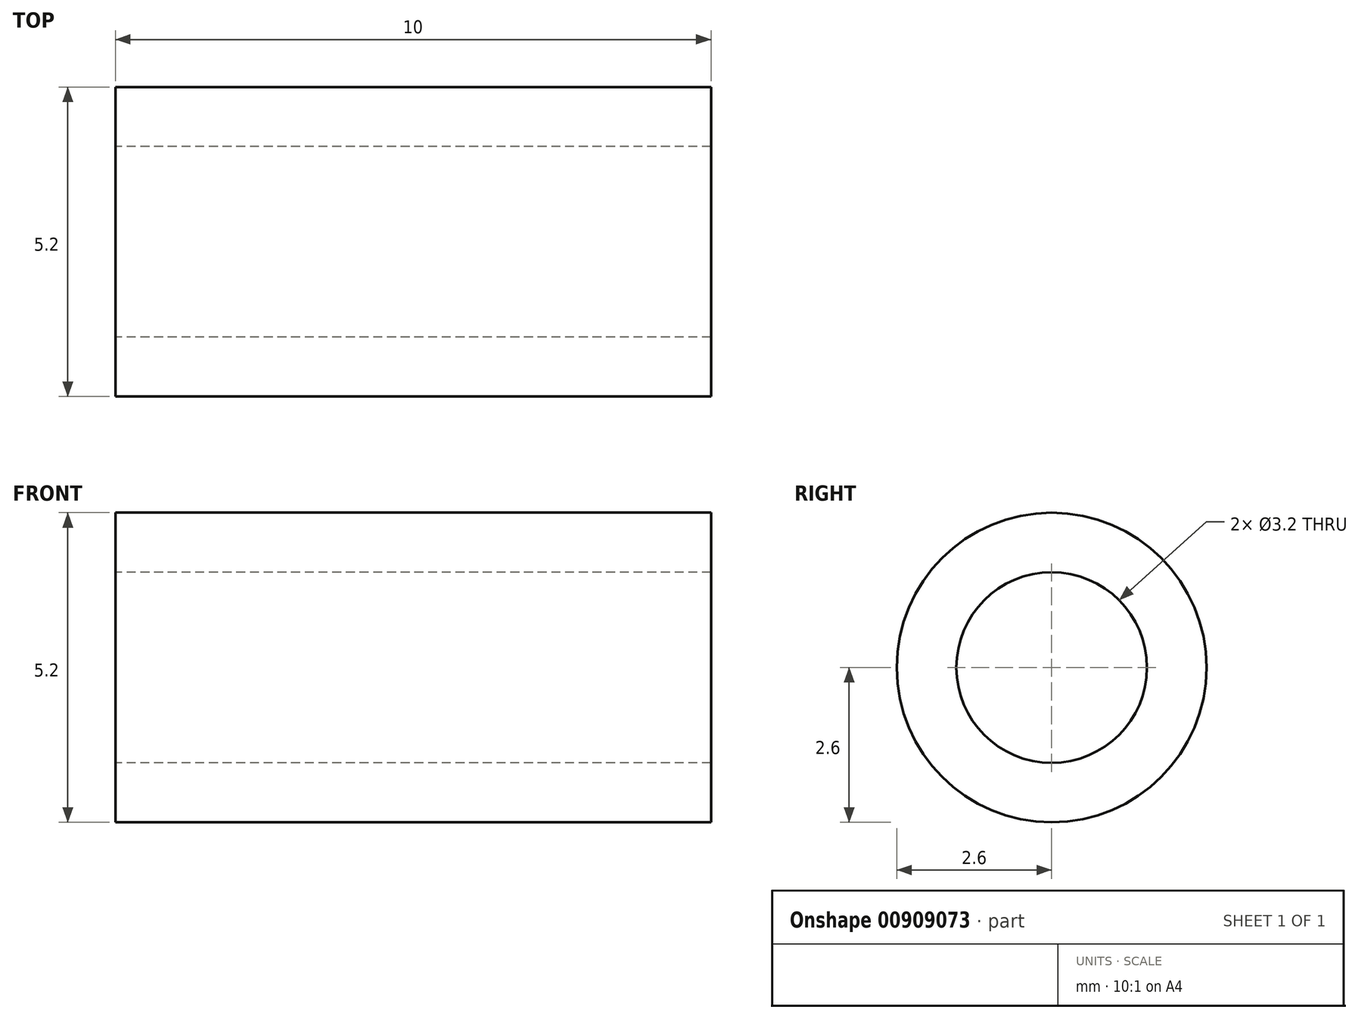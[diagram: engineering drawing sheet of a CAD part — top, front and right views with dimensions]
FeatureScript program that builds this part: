
annotation { "Feature Type Name" : "Feature", "Feature Type Description" : "" }
export const myFeature = defineFeature(function(context is Context, id is Id, definition is map)
    precondition{}
    {
        {
            var Q0;
            Q0=qCreatedBy(makeId("Right.planeOp"),FACE);
            var sketch = newSketch(context, id + "F0", { "sketchPlane" : qUnion([Q0])});
            skCircle(sketch, "E0", {"center": v(0, 0) * mm, "radius": 1.6 * mm});
            skCircle(sketch, "E1", {"center": v(0, 0) * mm, "radius": 2.6 * mm});
            skSolve(sketch);
        }
        {
            var Q0;
            Q0 = qSketchRegion(id + "F0", true);
            extrude(context, id + "F1", {"entities" : qUnion([Q0]), "depth" : 10 * mm, "offsetDistance" : 25 * mm});
        }
    });
